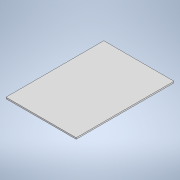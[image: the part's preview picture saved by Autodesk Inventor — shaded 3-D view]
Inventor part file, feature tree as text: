
AUTODESK INVENTOR PART (.ipt)
format: ipt  version: 2021 (Build 250183000, 183)  size: 90,624 bytes
history: native  units: in
note: dims shown in document units (in); Inventor stores cm internally (conversion verified against a paired STEP export)
features: extrude x1, sketch x1
ambient origin geometry x8: Origin, YZ Plane, XZ Plane, XY Plane, X Axis, Y Axis, Z Axis, Center Point
bodies: Solid1 (feature_tree)
feature tree (2):
  extrude  "Extrusion1"  Depth=7.0in
  sketch  "Sketch1"  dims[d0=5.024in d1=7.0in d2=0.1in d3=0.0in]
